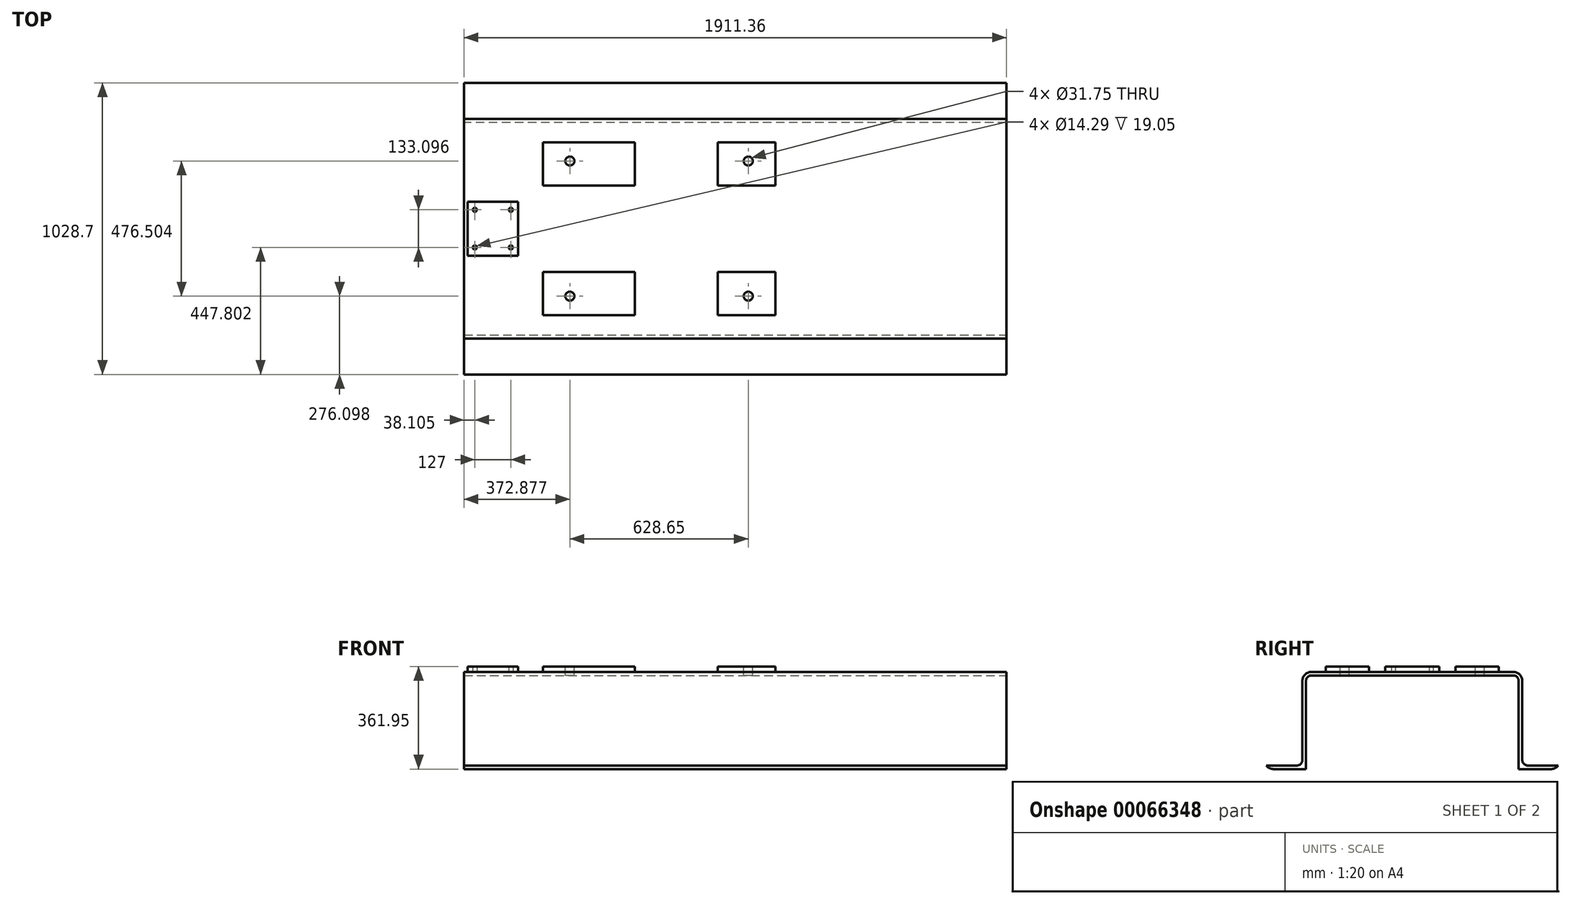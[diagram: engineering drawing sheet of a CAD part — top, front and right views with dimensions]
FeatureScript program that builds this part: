
annotation { "Feature Type Name" : "Feature", "Feature Type Description" : "" }
export const myFeature = defineFeature(function(context is Context, id is Id, definition is map)
    precondition{}
    {
        {
            var Q0;
            Q0=qCreatedBy(makeId("Top.planeOp"),FACE);
            var sketch = newSketch(context, id + "F0", { "sketchPlane" : qUnion([Q0])});
            skLineSegment(sketch, "E0.rect.bottom", {"start": v(-955.68, 387.35) * mm, "end": v(955.68, 387.35) * mm});
            skLineSegment(sketch, "E0.rect.top", {"start": v(-955.68, -387.35) * mm, "end": v(955.68, -387.35) * mm});
            skLineSegment(sketch, "E0.rect.left", {"start": v(-955.68, 387.35) * mm, "end": v(-955.68, -387.35) * mm});
            skLineSegment(sketch, "E0.rect.right", {"start": v(955.68, 387.35) * mm, "end": v(955.68, -387.35) * mm});
            skPoint(sketch, "E0.rect.middle", {"position": v(0, 0) * mm});
            skLineSegment(sketch, "E1.0", {"start": v(644.53, 387.35) * mm, "end": v(644.52, -387.35) * mm, "construction": true});
            skLineSegment(sketch, "E2.0", {"start": v(-268.35, 387.35) * mm, "end": v(-268.35, -387.35) * mm, "construction": true});
            skLineSegment(sketch, "E3.0", {"start": v(-354.2, 387.35) * mm, "end": v(-354.2, -387.35) * mm, "construction": true});
            skLineSegment(sketch, "E4.0", {"start": v(-678.05, 387.35) * mm, "end": v(-678.05, -387.35) * mm, "construction": true});
            skLineSegment(sketch, "E5.0", {"start": v(-62.1, 387.35) * mm, "end": v(-62.1, -387.35) * mm, "construction": true});
            skLineSegment(sketch, "E6.0", {"start": v(141.1, 387.35) * mm, "end": v(141.1, -387.35) * mm, "construction": true});
            skLineSegment(sketch, "E7", {"start": v(-955.68, 0) * mm, "end": v(955.68, 0) * mm, "construction": true});
            skLineSegment(sketch, "E8.0", {"start": v(-955.68, -152.4) * mm, "end": v(955.68, -152.4) * mm, "construction": true});
            skLineSegment(sketch, "E9.0", {"start": v(-955.68, -304.8) * mm, "end": v(955.68, -304.8) * mm, "construction": true});
            skLineSegment(sketch, "E10.bottom", {"start": v(-678.05, -152.4) * mm, "end": v(-354.2, -152.4) * mm});
            skLineSegment(sketch, "E10.top", {"start": v(-678.05, -304.8) * mm, "end": v(-354.2, -304.8) * mm});
            skLineSegment(sketch, "E10.left", {"start": v(-678.05, -152.4) * mm, "end": v(-678.05, -304.8) * mm});
            skLineSegment(sketch, "E10.right", {"start": v(-354.2, -152.4) * mm, "end": v(-354.2, -304.8) * mm});
            skLineSegment(sketch, "E11.bottom", {"start": v(-62.1, -152.4) * mm, "end": v(141.1, -152.4) * mm});
            skLineSegment(sketch, "E11.top", {"start": v(-62.1, -304.8) * mm, "end": v(141.1, -304.8) * mm});
            skLineSegment(sketch, "E11.left", {"start": v(-62.1, -152.4) * mm, "end": v(-62.1, -304.8) * mm});
            skLineSegment(sketch, "E11.right", {"start": v(141.1, -152.4) * mm, "end": v(141.1, -304.8) * mm});
            skLineSegment(sketch, "E12.0", {"start": v(-582.8, 387.35) * mm, "end": v(-582.8, -387.35) * mm, "construction": true});
            skLineSegment(sketch, "E13.0", {"start": v(45.85, 387.35) * mm, "end": v(45.85, -387.35) * mm, "construction": true});
            skLineSegment(sketch, "E14.0", {"start": v(-955.68, -238.25) * mm, "end": v(955.68, -238.25) * mm, "construction": true});
            skCircle(sketch, "E15", {"center": v(-582.8, -238.25) * mm, "radius": 15.88 * mm});
            skCircle(sketch, "E16", {"center": v(45.85, -238.25) * mm, "radius": 15.88 * mm});
            skLineSegment(sketch, "E17.MirrorCS", {"start": v(-354.2, 152.4) * mm, "end": v(-354.2, 304.8) * mm});
            skLineSegment(sketch, "E18.MirrorCS", {"start": v(-62.1, 304.8) * mm, "end": v(141.1, 304.8) * mm});
            skLineSegment(sketch, "E19.MirrorCS", {"start": v(141.1, 152.4) * mm, "end": v(141.1, 304.8) * mm});
            skCircle(sketch, "E20.MirrorC", {"center": v(45.85, 238.25) * mm, "radius": 15.88 * mm});
            skCircle(sketch, "E21.MirrorC", {"center": v(-582.8, 238.25) * mm, "radius": 15.88 * mm});
            skLineSegment(sketch, "E22.MirrorCS", {"start": v(-62.1, 152.4) * mm, "end": v(-62.1, 304.8) * mm});
            skLineSegment(sketch, "E23.MirrorCS", {"start": v(-678.05, 152.4) * mm, "end": v(-354.2, 152.4) * mm});
            skLineSegment(sketch, "E24.MirrorCS", {"start": v(-678.05, 152.4) * mm, "end": v(-678.05, 304.8) * mm});
            skLineSegment(sketch, "E25.MirrorCS", {"start": v(-62.1, 152.4) * mm, "end": v(141.1, 152.4) * mm});
            skLineSegment(sketch, "E26.MirrorCS", {"start": v(-678.05, 304.8) * mm, "end": v(-354.2, 304.8) * mm});
            skSolve(sketch);
        }
        {
            var Q0;
            Q0=makeQuery(id+"F0.imprint","IMPRINT",FACE,{"disambiguationData":[TD([[makeQuery(id+"F0.imprint","IMPRINT",EDGE,{"derivedFrom":sQuery(id+"F0.wireOp",EDGE,"E0.rect.bottom")}),-1.0]])]});
            var Q1;
            Q1=makeQuery(id+"F0.imprint","IMPRINT",FACE,{"disambiguationData":[TD([[makeQuery(id+"F0.imprint","IMPRINT",EDGE,{"derivedFrom":sQuery(id+"F0.wireOp",EDGE,"E17.MirrorCS")}),1.0]])]});
            var Q2;
            Q2=makeQuery(id+"F0.imprint","IMPRINT",FACE,{"disambiguationData":[TD([[makeQuery(id+"F0.imprint","IMPRINT",EDGE,{"derivedFrom":sQuery(id+"F0.wireOp",EDGE,"E10.bottom")}),-1.0]])]});
            var Q3;
            Q3=makeQuery(id+"F0.imprint","IMPRINT",FACE,{"disambiguationData":[TD([[makeQuery(id+"F0.imprint","IMPRINT",EDGE,{"derivedFrom":sQuery(id+"F0.wireOp",EDGE,"E18.MirrorCS")}),-1.0]])]});
            var Q4;
            Q4=makeQuery(id+"F0.imprint","IMPRINT",FACE,{"disambiguationData":[TD([[makeQuery(id+"F0.imprint","IMPRINT",EDGE,{"derivedFrom":sQuery(id+"F0.wireOp",EDGE,"E11.bottom")}),-1.0]])]});
            extrude(context, id + "F1", {"entities" : qUnion([Q0, Q1, Q2, Q3, Q4]), "oppositeDirection" : true, "depth" : 12.7 * mm});
        }
        {
            var Q0;
            Q0=makeQuery(id+"F0.imprint","IMPRINT",FACE,{"disambiguationData":[TD([[makeQuery(id+"F0.imprint","IMPRINT",EDGE,{"derivedFrom":sQuery(id+"F0.wireOp",EDGE,"E17.MirrorCS")}),1.0]])]});
            var Q1;
            Q1=makeQuery(id+"F0.imprint","IMPRINT",FACE,{"disambiguationData":[TD([[makeQuery(id+"F0.imprint","IMPRINT",EDGE,{"derivedFrom":sQuery(id+"F0.wireOp",EDGE,"E10.bottom")}),-1.0]])]});
            var Q2;
            Q2=makeQuery(id+"F0.imprint","IMPRINT",FACE,{"disambiguationData":[TD([[makeQuery(id+"F0.imprint","IMPRINT",EDGE,{"derivedFrom":sQuery(id+"F0.wireOp",EDGE,"E18.MirrorCS")}),-1.0]])]});
            var Q3;
            Q3=makeQuery(id+"F0.imprint","IMPRINT",FACE,{"disambiguationData":[TD([[makeQuery(id+"F0.imprint","IMPRINT",EDGE,{"derivedFrom":sQuery(id+"F0.wireOp",EDGE,"E11.bottom")}),-1.0]])]});
            extrude(context, id + "F2", {"entities" : qUnion([Q0, Q1, Q2, Q3]), "operationType" : NewBodyOperationType.ADD, "depth" : 19.05 * mm});
        }
        {
            var Q0;
            Q0=makeQuery(id+"F1.opExtrude","SWEPT_FACE",FACE,{"disambiguationData":[OSD([sQuery(id+"F0.wireOp",EDGE,"E0.rect.right")])]});
            var sketch = newSketch(context, id + "F3", { "sketchPlane" : qUnion([Q0])});
            skLineSegment(sketch, "E27.bottom", {"start": v(-387.35, 0) * mm, "end": v(-374.65, 0) * mm});
            skLineSegment(sketch, "E27.top", {"start": v(-387.35, -342.9) * mm, "end": v(-374.65, -342.9) * mm});
            skLineSegment(sketch, "E27.left", {"start": v(-387.35, 0) * mm, "end": v(-387.35, -342.9) * mm});
            skLineSegment(sketch, "E27.right", {"start": v(-374.65, 0) * mm, "end": v(-374.65, -342.9) * mm});
            skLineSegment(sketch, "E28", {"start": v(0, 0) * mm, "end": v(0, -288.05) * mm, "construction": true});
            skPoint(sketch, "E28.endSnap0", {"position": v(0, -12.7) * mm});
            skLineSegment(sketch, "E29.bottom", {"start": v(-374.65, -342.9) * mm, "end": v(-514.35, -342.9) * mm});
            skLineSegment(sketch, "E29.top", {"start": v(-374.65, -330.2) * mm, "end": v(-514.35, -330.2) * mm});
            skLineSegment(sketch, "E29.left", {"start": v(-374.65, -342.9) * mm, "end": v(-374.65, -330.2) * mm});
            skLineSegment(sketch, "E29.right", {"start": v(-514.35, -342.9) * mm, "end": v(-514.35, -330.2) * mm});
            skLineSegment(sketch, "E30.MirrorCS", {"start": v(387.35, 0) * mm, "end": v(374.65, 0) * mm});
            skLineSegment(sketch, "E31.MirrorCS", {"start": v(374.65, -342.9) * mm, "end": v(374.65, -330.2) * mm});
            skLineSegment(sketch, "E32.MirrorCS", {"start": v(387.35, -342.9) * mm, "end": v(374.65, -342.9) * mm});
            skLineSegment(sketch, "E33.MirrorCS", {"start": v(514.35, -342.9) * mm, "end": v(514.35, -330.2) * mm});
            skLineSegment(sketch, "E34.MirrorCS", {"start": v(387.35, 0) * mm, "end": v(387.35, -342.9) * mm});
            skLineSegment(sketch, "E35.MirrorCS", {"start": v(374.65, 0) * mm, "end": v(374.65, -342.9) * mm});
            skLineSegment(sketch, "E36.MirrorCS", {"start": v(374.65, -330.2) * mm, "end": v(514.35, -330.2) * mm});
            skLineSegment(sketch, "E37.MirrorCS", {"start": v(374.65, -342.9) * mm, "end": v(514.35, -342.9) * mm});
            skSolve(sketch);
        }
        {
            var Q0;
            Q0=qSketchRegion(id+"F3",true);
            extrude(context, id + "F4", {"entities" : qUnion([Q0]), "operationType" : NewBodyOperationType.ADD, "oppositeDirection" : true, "depth" : 1911.35 * mm});
        }
        {
            var Q0;
            Q0=makeQuery(id+"F4.opExtrude","SWEPT_EDGE",EDGE,{"disambiguationData":[OSD([sQuery(id+"F3.wireOp",EDGE,"E27.left"),sQuery(id+"F3.wireOp",EDGE,"E29.top")])]});
            var Q1;
            Q1=makeQuery(id+"F4.opExtrude","SWEPT_EDGE",EDGE,{"disambiguationData":[OSD([sQuery(id+"F3.wireOp",EDGE,"E34.MirrorCS"),sQuery(id+"F3.wireOp",EDGE,"E36.MirrorCS")])]});
            var Q2;
            Q2=makeQuery(id+"F4.boolean.opBoolean","INTERSECT",EDGE,{"derivedFrom":[makeQuery(id+"F1.opExtrude","CAP_FACE",FACE,{"disambiguationData":[OSD([sQuery(id+"F0.wireOp",EDGE,"E0.rect.bottom"),sQuery(id+"F0.wireOp",EDGE,"E0.rect.top"),sQuery(id+"F0.wireOp",EDGE,"E0.rect.left"),sQuery(id+"F0.wireOp",EDGE,"E0.rect.right"),sQuery(id+"F0.wireOp",EDGE,"E15"),sQuery(id+"F0.wireOp",EDGE,"E16"),sQuery(id+"F0.wireOp",EDGE,"E20.MirrorC"),sQuery(id+"F0.wireOp",EDGE,"E21.MirrorC")])],"isStart":false}),makeQuery(id+"F4.opExtrude","SWEPT_FACE",FACE,{"disambiguationData":[OSD([sQuery(id+"F3.wireOp",EDGE,"E35.MirrorCS")])]})]});
            var Q3;
            Q3=makeQuery(id+"F4.boolean.opBoolean","INTERSECT",EDGE,{"derivedFrom":[makeQuery(id+"F1.opExtrude","CAP_FACE",FACE,{"disambiguationData":[OSD([sQuery(id+"F0.wireOp",EDGE,"E0.rect.bottom"),sQuery(id+"F0.wireOp",EDGE,"E0.rect.top"),sQuery(id+"F0.wireOp",EDGE,"E0.rect.left"),sQuery(id+"F0.wireOp",EDGE,"E0.rect.right"),sQuery(id+"F0.wireOp",EDGE,"E15"),sQuery(id+"F0.wireOp",EDGE,"E16"),sQuery(id+"F0.wireOp",EDGE,"E20.MirrorC"),sQuery(id+"F0.wireOp",EDGE,"E21.MirrorC")])],"isStart":false}),makeQuery(id+"F4.opExtrude","SWEPT_FACE",FACE,{"disambiguationData":[OSD([sQuery(id+"F3.wireOp",EDGE,"E27.right"),sQuery(id+"F3.wireOp",EDGE,"E29.left")])]})]});
            fillet(context, id + "F5", {"entities" : qUnion([Q0, Q1, Q2, Q3]), "radius" : 19.05 * mm, "tangentPropagation" : true, "allowEdgeOverflow" : false});
        }
        {
            var Q0;
            Q0=makeQuery(id+"F4.opExtrude","SWEPT_EDGE",EDGE,{"disambiguationData":[OSD([sQuery(id+"F3.wireOp",EDGE,"E35.MirrorCS"),sQuery(id+"F3.wireOp",EDGE,"E37.MirrorCS")])]});
            var Q1;
            Q1=makeQuery(id+"F4.opExtrude","SWEPT_EDGE",EDGE,{"disambiguationData":[OSD([sQuery(id+"F3.wireOp",EDGE,"E29.bottom"),sQuery(id+"F3.wireOp",EDGE,"E29.left")])]});
            var Q2;
            Q2=makeQuery(id+"F1.opExtrude","CAP_EDGE",EDGE,{"disambiguationData":[OSD([sQuery(id+"F0.wireOp",EDGE,"E0.rect.bottom")])],"isStart":true});
            var Q3;
            Q3=makeQuery(id+"F1.opExtrude","CAP_EDGE",EDGE,{"disambiguationData":[OSD([sQuery(id+"F0.wireOp",EDGE,"E0.rect.top")])],"isStart":true});
            fillet(context, id + "F6", {"entities" : qUnion([Q0, Q1, Q2, Q3]), "radius" : 31.75 * mm, "tangentPropagation" : true, "allowEdgeOverflow" : false});
        }
        {
            var Q0;
            Q0=makeQuery(id+"F0.imprint","IMPRINT",FACE,{"disambiguationData":[TD([[makeQuery(id+"F0.imprint","IMPRINT",EDGE,{"derivedFrom":sQuery(id+"F0.wireOp",EDGE,"E0.rect.bottom")}),-1.0]])]});
            var sketch = newSketch(context, id + "F7", { "sketchPlane" : qUnion([Q0])});
            skLineSegment(sketch, "E38.0", {"start": v(-268.35, 387.35) * mm, "end": v(-268.35, -387.35) * mm, "construction": true});
            skLineSegment(sketch, "E39.0", {"start": v(-678.05, 152.4) * mm, "end": v(-678.05, 304.8) * mm, "construction": true});
            skLineSegment(sketch, "E40.0", {"start": v(-765.43, 0) * mm, "end": v(955.68, 0) * mm, "construction": true});
            skLineSegment(sketch, "E41.0", {"start": v(-765.43, 0) * mm, "end": v(-765.43, 95.25) * mm});
            skLineSegment(sketch, "E42.0", {"start": v(-943.23, 0) * mm, "end": v(-943.23, 95.25) * mm});
            skLineSegment(sketch, "E43.0", {"start": v(-943.23, 95.25) * mm, "end": v(-765.43, 95.25) * mm});
            skPoint(sketch, "E44.orphan", {"position": v(-955.68, 0) * mm});
            skLineSegment(sketch, "E45.MirrorCS", {"start": v(-943.23, -95.25) * mm, "end": v(-765.43, -95.25) * mm});
            skLineSegment(sketch, "E46.MirrorCS", {"start": v(-765.43, 0) * mm, "end": v(-765.43, -95.25) * mm});
            skLineSegment(sketch, "E47.MirrorCS", {"start": v(-943.23, 0) * mm, "end": v(-943.23, -95.25) * mm});
            skPoint(sketch, "E48.orphan", {"position": v(-955.68, 95.25) * mm});
            skPoint(sketch, "E49.orphan", {"position": v(-955.68, -95.25) * mm});
            skLineSegment(sketch, "E50.0", {"start": v(-790.57, 387.35) * mm, "end": v(-790.58, -387.35) * mm, "construction": true});
            skLineSegment(sketch, "E51.0", {"start": v(-917.57, 387.35) * mm, "end": v(-917.58, -387.35) * mm, "construction": true});
            skLineSegment(sketch, "E52.0", {"start": v(-943.23, -66.55) * mm, "end": v(955.68, -66.55) * mm, "construction": true});
            skCircle(sketch, "E53", {"center": v(-917.57, -66.55) * mm, "radius": 7.14 * mm});
            skCircle(sketch, "E54", {"center": v(-790.57, -66.55) * mm, "radius": 7.14 * mm});
            skCircle(sketch, "E55.MirrorC", {"center": v(-790.57, 66.55) * mm, "radius": 7.14 * mm});
            skCircle(sketch, "E56.MirrorC", {"center": v(-917.57, 66.55) * mm, "radius": 7.14 * mm});
            skSolve(sketch);
        }
        {
            var Q0;
            Q0=qSketchRegion(id+"F7",true);
            extrude(context, id + "F8", {"entities" : qUnion([Q0]), "operationType" : NewBodyOperationType.ADD, "depth" : 19.05 * mm});
        }
    });
